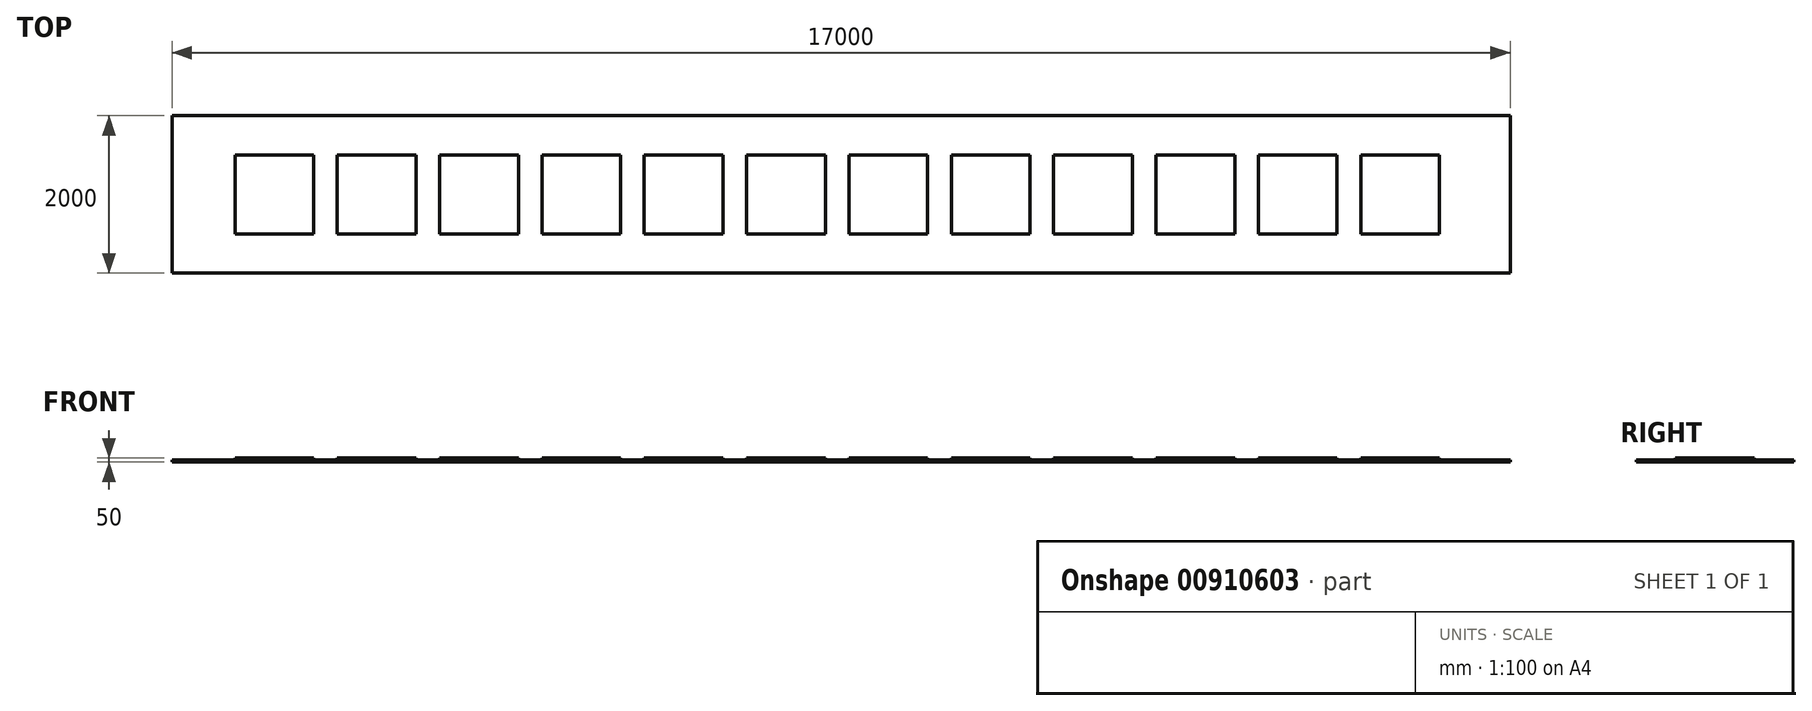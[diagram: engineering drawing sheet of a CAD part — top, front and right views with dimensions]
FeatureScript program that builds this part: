
annotation { "Feature Type Name" : "Feature", "Feature Type Description" : "" }
export const myFeature = defineFeature(function(context is Context, id is Id, definition is map)
    precondition{}
    {
        {
            var Q0;
            Q0=qCreatedBy(makeId("Top.planeOp"),FACE);
            var sketch = newSketch(context, id + "F0", { "sketchPlane" : qUnion([Q0])});
            skLineSegment(sketch, "E0.bottom", {"start": v(0, 0) * mm, "end": v(-17000, 0) * mm});
            skLineSegment(sketch, "E0.top", {"start": v(0, 2000) * mm, "end": v(-17000, 2000) * mm});
            skLineSegment(sketch, "E0.left", {"start": v(0, 0) * mm, "end": v(0, 2000) * mm});
            skLineSegment(sketch, "E0.right", {"start": v(-17000, 0) * mm, "end": v(-17000, 2000) * mm});
            skSolve(sketch);
        }
        {
            var Q0;
            Q0=makeQuery(id+"F0.imprint","IMPRINT",FACE,{"disambiguationData":[TD([[makeQuery(id+"F0.imprint","IMPRINT",EDGE,{"derivedFrom":sQuery(id+"F0.wireOp",EDGE,"E0.bottom")}),-1.0]])]});
            extrude(context, id + "F1", {"entities" : qUnion([Q0]), "depth" : 25 * mm, "offsetDistance" : 25 * mm});
        }
        {
            var Q0;
            Q0=makeQuery(id+"F1.opExtrude","CAP_FACE",FACE,{"disambiguationData":[OSD([sQuery(id+"F0.wireOp",EDGE,"E0.bottom"),sQuery(id+"F0.wireOp",EDGE,"E0.top"),sQuery(id+"F0.wireOp",EDGE,"E0.left"),sQuery(id+"F0.wireOp",EDGE,"E0.right")])],"isStart":false});
            var sketch = newSketch(context, id + "F2", { "sketchPlane" : qUnion([Q0])});
            skLineSegment(sketch, "E1", {"start": v(-1400, 0) * mm, "end": v(0, 0) * mm});
            skLineSegment(sketch, "E2.bottom", {"start": v(-15200, 500) * mm, "end": v(-16200, 500) * mm});
            skLineSegment(sketch, "E2.top", {"start": v(-15200, 1500) * mm, "end": v(-16200, 1500) * mm});
            skLineSegment(sketch, "E2.left", {"start": v(-15200, 500) * mm, "end": v(-15200, 1500) * mm});
            skLineSegment(sketch, "E2.right", {"start": v(-16200, 500) * mm, "end": v(-16200, 1500) * mm});
            skPoint(sketch, "E2.middle", {"position": v(-15700, 1000) * mm});
            skLineSegment(sketch, "E3.bottom", {"start": v(-13900, 500) * mm, "end": v(-14900, 500) * mm});
            skLineSegment(sketch, "E3.top", {"start": v(-13900, 1500) * mm, "end": v(-14900, 1500) * mm});
            skLineSegment(sketch, "E3.left", {"start": v(-13900, 500) * mm, "end": v(-13900, 1500) * mm});
            skLineSegment(sketch, "E3.right", {"start": v(-14900, 500) * mm, "end": v(-14900, 1500) * mm});
            skPoint(sketch, "E3.middle", {"position": v(-14400, 1000) * mm});
            skLineSegment(sketch, "E4.bottom", {"start": v(-12600, 500) * mm, "end": v(-13600, 500) * mm});
            skLineSegment(sketch, "E4.top", {"start": v(-12600, 1500) * mm, "end": v(-13600, 1500) * mm});
            skLineSegment(sketch, "E4.left", {"start": v(-12600, 500) * mm, "end": v(-12600, 1500) * mm});
            skLineSegment(sketch, "E4.right", {"start": v(-13600, 500) * mm, "end": v(-13600, 1500) * mm});
            skPoint(sketch, "E4.middle", {"position": v(-13100, 1000) * mm});
            skLineSegment(sketch, "E5.bottom", {"start": v(-11300, 500) * mm, "end": v(-12300, 500) * mm});
            skLineSegment(sketch, "E5.top", {"start": v(-11300, 1500) * mm, "end": v(-12300, 1500) * mm});
            skLineSegment(sketch, "E5.left", {"start": v(-11300, 500) * mm, "end": v(-11300, 1500) * mm});
            skLineSegment(sketch, "E5.right", {"start": v(-12300, 500) * mm, "end": v(-12300, 1500) * mm});
            skPoint(sketch, "E5.middle", {"position": v(-11800, 1000) * mm});
            skLineSegment(sketch, "E6.bottom", {"start": v(-10000, 500) * mm, "end": v(-11000, 500) * mm});
            skLineSegment(sketch, "E6.top", {"start": v(-10000, 1500) * mm, "end": v(-11000, 1500) * mm});
            skLineSegment(sketch, "E6.left", {"start": v(-10000, 500) * mm, "end": v(-10000, 1500) * mm});
            skLineSegment(sketch, "E6.right", {"start": v(-11000, 500) * mm, "end": v(-11000, 1500) * mm});
            skPoint(sketch, "E6.middle", {"position": v(-10500, 1000) * mm});
            skLineSegment(sketch, "E7.bottom", {"start": v(-8700, 500) * mm, "end": v(-9700, 500) * mm});
            skLineSegment(sketch, "E7.top", {"start": v(-8700, 1500) * mm, "end": v(-9700, 1500) * mm});
            skLineSegment(sketch, "E7.left", {"start": v(-8700, 500) * mm, "end": v(-8700, 1500) * mm});
            skLineSegment(sketch, "E7.right", {"start": v(-9700, 500) * mm, "end": v(-9700, 1500) * mm});
            skPoint(sketch, "E7.middle", {"position": v(-9200, 1000) * mm});
            skLineSegment(sketch, "E8.bottom", {"start": v(-7400, 500) * mm, "end": v(-8400, 500) * mm});
            skLineSegment(sketch, "E8.top", {"start": v(-7400, 1500) * mm, "end": v(-8400, 1500) * mm});
            skLineSegment(sketch, "E8.left", {"start": v(-7400, 500) * mm, "end": v(-7400, 1500) * mm});
            skLineSegment(sketch, "E8.right", {"start": v(-8400, 500) * mm, "end": v(-8400, 1500) * mm});
            skPoint(sketch, "E8.middle", {"position": v(-7900, 1000) * mm});
            skPoint(sketch, "E9.middle", {"position": v(-6600, 1000) * mm});
            skLineSegment(sketch, "E10.bottom", {"start": v(-6100, 500) * mm, "end": v(-7100, 500) * mm});
            skLineSegment(sketch, "E10.top", {"start": v(-6100, 1500) * mm, "end": v(-7100, 1500) * mm});
            skLineSegment(sketch, "E10.left", {"start": v(-6100, 500) * mm, "end": v(-6100, 1500) * mm});
            skLineSegment(sketch, "E10.right", {"start": v(-7100, 500) * mm, "end": v(-7100, 1500) * mm});
            skLineSegment(sketch, "E11.bottom", {"start": v(-4800, 500) * mm, "end": v(-5800, 500) * mm});
            skLineSegment(sketch, "E11.top", {"start": v(-4800, 1500) * mm, "end": v(-5800, 1500) * mm});
            skLineSegment(sketch, "E11.left", {"start": v(-4800, 500) * mm, "end": v(-4800, 1500) * mm});
            skLineSegment(sketch, "E11.right", {"start": v(-5800, 500) * mm, "end": v(-5800, 1500) * mm});
            skPoint(sketch, "E11.middle", {"position": v(-5300, 1000) * mm});
            skLineSegment(sketch, "E12.bottom", {"start": v(-3500, 500) * mm, "end": v(-4500, 500) * mm});
            skLineSegment(sketch, "E12.top", {"start": v(-3500, 1500) * mm, "end": v(-4500, 1500) * mm});
            skLineSegment(sketch, "E12.left", {"start": v(-3500, 500) * mm, "end": v(-3500, 1500) * mm});
            skLineSegment(sketch, "E12.right", {"start": v(-4500, 500) * mm, "end": v(-4500, 1500) * mm});
            skPoint(sketch, "E12.middle", {"position": v(-4000, 1000) * mm});
            skLineSegment(sketch, "E13.bottom", {"start": v(-2200, 500) * mm, "end": v(-3200, 500) * mm});
            skLineSegment(sketch, "E13.top", {"start": v(-2200, 1500) * mm, "end": v(-3200, 1500) * mm});
            skLineSegment(sketch, "E13.left", {"start": v(-2200, 500) * mm, "end": v(-2200, 1500) * mm});
            skLineSegment(sketch, "E13.right", {"start": v(-3200, 500) * mm, "end": v(-3200, 1500) * mm});
            skPoint(sketch, "E13.middle", {"position": v(-2700, 1000) * mm});
            skLineSegment(sketch, "E14.bottom", {"start": v(-900, 500) * mm, "end": v(-1900, 500) * mm});
            skLineSegment(sketch, "E14.top", {"start": v(-900, 1500) * mm, "end": v(-1900, 1500) * mm});
            skLineSegment(sketch, "E14.left", {"start": v(-900, 500) * mm, "end": v(-900, 1500) * mm});
            skLineSegment(sketch, "E14.right", {"start": v(-1900, 500) * mm, "end": v(-1900, 1500) * mm});
            skPoint(sketch, "E14.middle", {"position": v(-1400, 1000) * mm});
            skLineSegment(sketch, "E15", {"start": v(-17000, 1000) * mm, "end": v(-16200, 1000) * mm});
            skLineSegment(sketch, "E16", {"start": v(-15200, 1000) * mm, "end": v(-14900, 1000) * mm});
            skLineSegment(sketch, "E17", {"start": v(-17000, 2000) * mm, "end": v(-17000, 0) * mm});
            skSolve(sketch);
        }
        {
            var Q0;
            {var subQ3=sQuery(id+"F2.wireOp",EDGE,"E2.bottom");Q0=makeQuery(id+"F2.imprint","IMPRINT",FACE,{"disambiguationData":[TD([[makeQuery(id+"F2.imprint","IMPRINT",EDGE,{"derivedFrom":subQ3}),-1.0]])]});}
            var Q1;
            {var subQ1=sQuery(id+"F2.wireOp",EDGE,"E3.bottom");Q1=makeQuery(id+"F2.imprint","IMPRINT",FACE,{"disambiguationData":[TD([[makeQuery(id+"F2.imprint","IMPRINT",EDGE,{"derivedFrom":subQ1}),-1.0]])]});}
            var Q2;
            Q2=makeQuery(id+"F2.imprint","IMPRINT",FACE,{"disambiguationData":[TD([[makeQuery(id+"F2.imprint","IMPRINT",EDGE,{"derivedFrom":sQuery(id+"F2.wireOp",EDGE,"E4.bottom")}),-1.0]])]});
            var Q3;
            Q3=makeQuery(id+"F2.imprint","IMPRINT",FACE,{"disambiguationData":[TD([[makeQuery(id+"F2.imprint","IMPRINT",EDGE,{"derivedFrom":sQuery(id+"F2.wireOp",EDGE,"E5.bottom")}),-1.0]])]});
            var Q4;
            Q4=makeQuery(id+"F2.imprint","IMPRINT",FACE,{"disambiguationData":[TD([[makeQuery(id+"F2.imprint","IMPRINT",EDGE,{"derivedFrom":sQuery(id+"F2.wireOp",EDGE,"E6.bottom")}),-1.0]])]});
            var Q5;
            Q5=makeQuery(id+"F2.imprint","IMPRINT",FACE,{"disambiguationData":[TD([[makeQuery(id+"F2.imprint","IMPRINT",EDGE,{"derivedFrom":sQuery(id+"F2.wireOp",EDGE,"E7.bottom")}),-1.0]])]});
            var Q6;
            Q6=makeQuery(id+"F2.imprint","IMPRINT",FACE,{"disambiguationData":[TD([[makeQuery(id+"F2.imprint","IMPRINT",EDGE,{"derivedFrom":sQuery(id+"F2.wireOp",EDGE,"E8.bottom")}),-1.0]])]});
            var Q7;
            Q7=makeQuery(id+"F2.imprint","IMPRINT",FACE,{"disambiguationData":[TD([[makeQuery(id+"F2.imprint","IMPRINT",EDGE,{"derivedFrom":sQuery(id+"F2.wireOp",EDGE,"E10.bottom")}),-1.0]])]});
            var Q8;
            Q8=makeQuery(id+"F2.imprint","IMPRINT",FACE,{"disambiguationData":[TD([[makeQuery(id+"F2.imprint","IMPRINT",EDGE,{"derivedFrom":sQuery(id+"F2.wireOp",EDGE,"E11.bottom")}),-1.0]])]});
            var Q9;
            Q9=makeQuery(id+"F2.imprint","IMPRINT",FACE,{"disambiguationData":[TD([[makeQuery(id+"F2.imprint","IMPRINT",EDGE,{"derivedFrom":sQuery(id+"F2.wireOp",EDGE,"E12.bottom")}),-1.0]])]});
            var Q10;
            Q10=makeQuery(id+"F2.imprint","IMPRINT",FACE,{"disambiguationData":[TD([[makeQuery(id+"F2.imprint","IMPRINT",EDGE,{"derivedFrom":sQuery(id+"F2.wireOp",EDGE,"E13.bottom")}),-1.0]])]});
            var Q11;
            Q11=makeQuery(id+"F2.imprint","IMPRINT",FACE,{"disambiguationData":[TD([[makeQuery(id+"F2.imprint","IMPRINT",EDGE,{"derivedFrom":sQuery(id+"F2.wireOp",EDGE,"E14.bottom")}),-1.0]])]});
            extrude(context, id + "F3", {"entities" : qUnion([Q0, Q1, Q2, Q3, Q4, Q5, Q6, Q7, Q8, Q9, Q10, Q11]), "operationType" : NewBodyOperationType.ADD, "depth" : 25 * mm, "offsetDistance" : 25 * mm});
        }
    });
